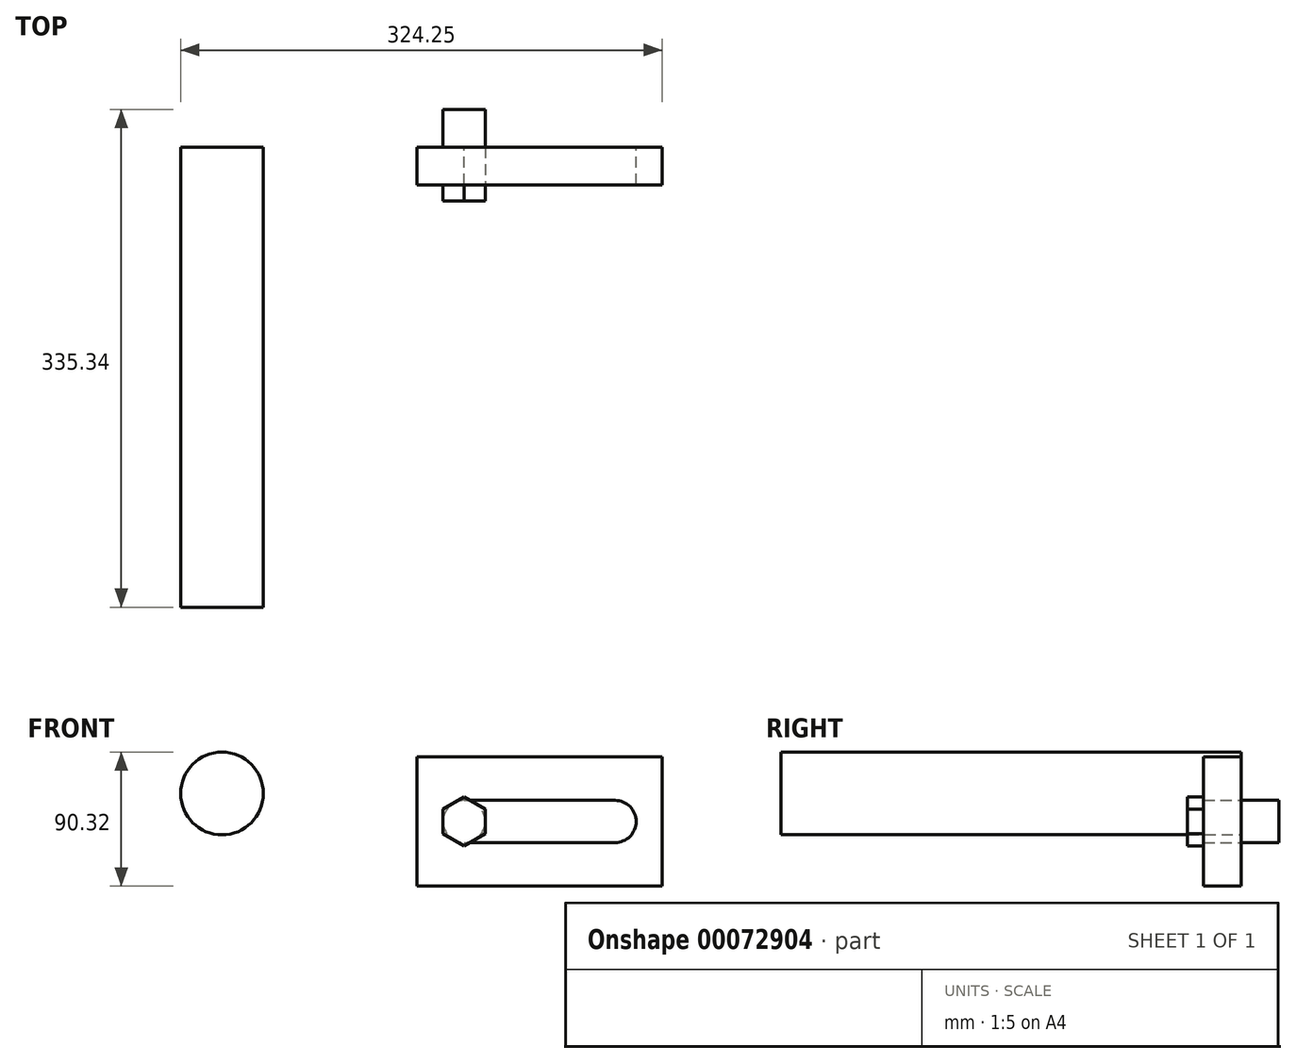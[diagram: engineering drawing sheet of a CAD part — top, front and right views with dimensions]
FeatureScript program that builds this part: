
annotation { "Feature Type Name" : "Feature", "Feature Type Description" : "" }
export const myFeature = defineFeature(function(context is Context, id is Id, definition is map)
    precondition{}
    {
        {
            var Q0;
            Q0=qCreatedBy(makeId("Front.planeOp"),FACE);
            var sketch = newSketch(context, id + "F0", { "sketchPlane" : qUnion([Q0])});
            skLineSegment(sketch, "E0.rect.bottom", {"start": v(-82.55, 43.58) * mm, "end": v(82.55, 43.58) * mm});
            skLineSegment(sketch, "E0.rect.top", {"start": v(-82.55, -43.58) * mm, "end": v(82.55, -43.58) * mm});
            skLineSegment(sketch, "E0.rect.left", {"start": v(-82.55, 43.58) * mm, "end": v(-82.55, -43.58) * mm});
            skLineSegment(sketch, "E0.rect.right", {"start": v(82.55, 43.58) * mm, "end": v(82.55, -43.58) * mm});
            skPoint(sketch, "E0.rect.middle", {"position": v(0, 0) * mm});
            skArc(sketch, "E1", {"start": v(-50.8, 14.23) * mm, "mid": v(-65.03, 0) * mm, "end": v(-50.8, -14.23) * mm});
            skLineSegment(sketch, "E2", {"start": v(0, 0) * mm, "end": v(0, 32.8) * mm, "construction": true});
            skArc(sketch, "E3.MirrorC", {"start": v(50.8, 14.23) * mm, "mid": v(65.03, 0) * mm, "end": v(50.8, -14.23) * mm});
            skLineSegment(sketch, "E4", {"start": v(-50.8, 14.23) * mm, "end": v(50.8, 14.23) * mm});
            skLineSegment(sketch, "E5", {"start": v(0, 0) * mm, "end": v(-18.67, 0) * mm, "construction": true});
            skLineSegment(sketch, "E6.MirrorCS", {"start": v(-50.8, -14.23) * mm, "end": v(50.8, -14.23) * mm});
            skSolve(sketch);
        }
        {
            var Q0;
            Q0 = qSketchRegion(id + "F0", true);
            extrude(context, id + "F1", {"entities" : qUnion([Q0]), "depth" : 25.4 * mm});
        }
        {
            var Q0;
            Q0=makeQuery(id+"F1.opExtrude","CAP_FACE",FACE,{"disambiguationData":[OSD([sQuery(id+"F0.wireOp",EDGE,"E0.rect.bottom"),sQuery(id+"F0.wireOp",EDGE,"E0.rect.top"),sQuery(id+"F0.wireOp",EDGE,"E0.rect.left"),sQuery(id+"F0.wireOp",EDGE,"E0.rect.right"),sQuery(id+"F0.wireOp",EDGE,"E1"),sQuery(id+"F0.wireOp",EDGE,"E3.MirrorC"),sQuery(id+"F0.wireOp",EDGE,"E4"),sQuery(id+"F0.wireOp",EDGE,"E6.MirrorCS")])],"isStart":false});
            var sketch = newSketch(context, id + "F2", { "sketchPlane" : qUnion([Q0])});
            skCircle(sketch, "E7.cCircle", {"center": v(-50.8, 0) * mm, "radius": 14.23 * mm, "construction": true});
            skLineSegment(sketch, "E7.0", {"start": v(-65.03, -8.21) * mm, "end": v(-65.03, 8.21) * mm});
            skLineSegment(sketch, "E7.1", {"start": v(-65.03, 8.21) * mm, "end": v(-50.8, 16.43) * mm});
            skLineSegment(sketch, "E7.2", {"start": v(-50.8, 16.43) * mm, "end": v(-36.57, 8.21) * mm});
            skLineSegment(sketch, "E7.3", {"start": v(-36.57, 8.21) * mm, "end": v(-36.57, -8.21) * mm});
            skLineSegment(sketch, "E7.4", {"start": v(-36.57, -8.21) * mm, "end": v(-50.8, -16.43) * mm});
            skLineSegment(sketch, "E7.5", {"start": v(-50.8, -16.43) * mm, "end": v(-65.03, -8.21) * mm});
            skPoint(sketch, "E7.0.midPoint", {"position": v(-65.03, 0) * mm});
            skSolve(sketch);
        }
        {
            var Q0;
            Q0 = qSketchRegion(id + "F2", true);
            extrude(context, id + "F3", {"entities" : qUnion([Q0]), "depth" : 10.8 * mm});
        }
        {
            var Q0;
            Q0=makeQuery(id+"F3.opExtrude","CAP_FACE",FACE,{"disambiguationData":[OSD([sQuery(id+"F2.wireOp",EDGE,"E7.0"),sQuery(id+"F2.wireOp",EDGE,"E7.1"),sQuery(id+"F2.wireOp",EDGE,"E7.2"),sQuery(id+"F2.wireOp",EDGE,"E7.3"),sQuery(id+"F2.wireOp",EDGE,"E7.4"),sQuery(id+"F2.wireOp",EDGE,"E7.5")])],"isStart":true});
            var sketch = newSketch(context, id + "F4", { "sketchPlane" : qUnion([Q0])});
            skArc(sketch, "E8.0", {"start": v(50.8, 14.23) * mm, "mid": v(65.03, 0) * mm, "end": v(50.8, -14.23) * mm});
            skLineSegment(sketch, "E9", {"start": v(50.8, 14.23) * mm, "end": v(50.8, 0) * mm, "construction": true});
            skArc(sketch, "E10.MirrorCS", {"start": v(50.8, 14.23) * mm, "mid": v(36.57, 0) * mm, "end": v(50.8, -14.23) * mm});
            skSolve(sketch);
        }
        {
            var Q0;
            Q0 = qSketchRegion(id + "F4", true);
            extrude(context, id + "F5", {"entities" : qUnion([Q0]), "operationType" : NewBodyOperationType.ADD, "depth" : 50.8 * mm});
        }
        {
            var Q0;
            Q0=qCreatedBy(makeId("Front.planeOp"),FACE);
            var sketch = newSketch(context, id + "F6", { "sketchPlane" : qUnion([Q0])});
            skCircle(sketch, "E11", {"center": v(-213.84, 18.88) * mm, "radius": 27.86 * mm});
            skSolve(sketch);
        }
        {
            var Q0;
            Q0 = qSketchRegion(id + "F6", true);
            extrude(context, id + "F7", {"entities" : qUnion([Q0]), "depth" : 309.94 * mm});
        }
        {
            var Q0;
            Q0=makeQuery(id+"F7.opExtrude","CAP_EDGE",EDGE,{"disambiguationData":[OSD([sQuery(id+"F6.wireOp",EDGE,"E11")])],"isStart":false});
            var Q1;
            Q1=qCreatedBy(makeId("Right.planeOp"),FACE);
            cPlane(context, id + "F8", {"entities" : qUnion([Q0, Q1]), "cplaneType" : CPlaneType.LINE_ANGLE, "offset" : 152.4 * mm, "angle" : 0 * degree, "width" : 152.4 * mm, "height" : 152.4 * mm});
        }
    });
